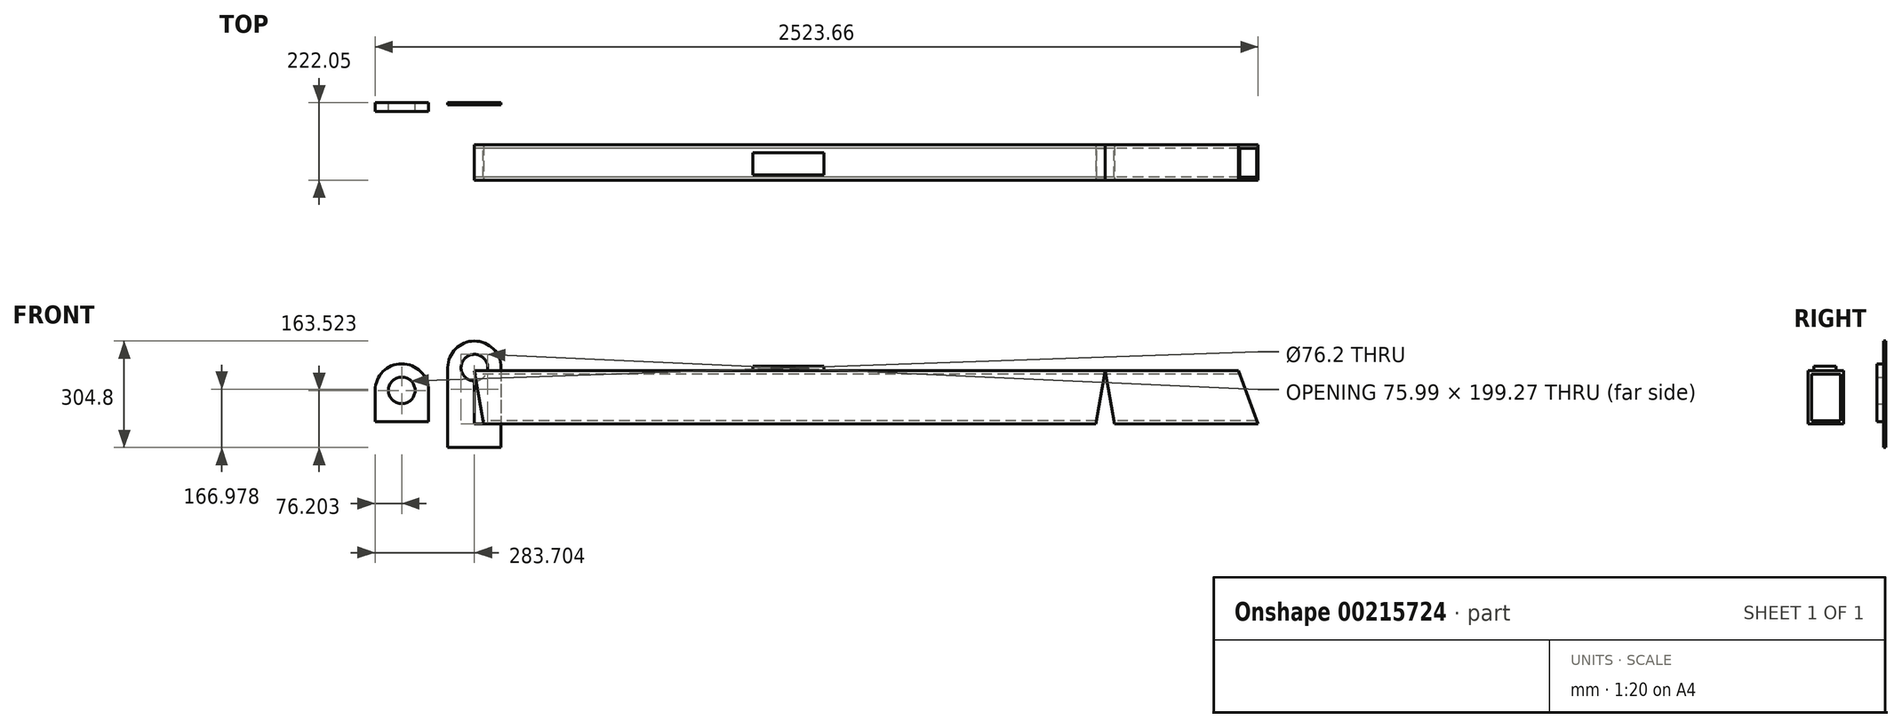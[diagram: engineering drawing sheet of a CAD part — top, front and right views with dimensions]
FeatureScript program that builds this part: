
annotation { "Feature Type Name" : "Feature", "Feature Type Description" : "" }
export const myFeature = defineFeature(function(context is Context, id is Id, definition is map)
    precondition{}
    {
        {
            var Q0;
            Q0=qCreatedBy(makeId("Front.planeOp"),FACE);
            var sketch = newSketch(context, id + "F0", { "sketchPlane" : qUnion([Q0])});
            skLineSegment(sketch, "E0.bottom", {"start": v(0, 152.4) * mm, "end": v(0, 152.4) * mm});
            skLineSegment(sketch, "E0.top", {"start": v(76.2, -152.4) * mm, "end": v(-76.2, -152.4) * mm});
            skLineSegment(sketch, "E0.left", {"start": v(76.2, 76.2) * mm, "end": v(76.2, -152.4) * mm});
            skLineSegment(sketch, "E0.right", {"start": v(-76.2, 76.2) * mm, "end": v(-76.2, -152.4) * mm});
            skPoint(sketch, "E0.middle", {"position": v(0, 0) * mm});
            skPoint(sketch, "E1.visualSharp", {"position": v(-76.2, 152.4) * mm});
            skArc(sketch, "E1.filletArc", {"start": v(0, 152.4) * mm, "mid": v(-53.88, 130.08) * mm, "end": v(-76.2, 76.2) * mm});
            skPoint(sketch, "E2.visualSharp", {"position": v(76.2, 152.4) * mm});
            skArc(sketch, "E2.filletArc", {"start": v(76.2, 76.2) * mm, "mid": v(53.88, 130.08) * mm, "end": v(0, 152.4) * mm});
            skCircle(sketch, "E3", {"center": v(0, 76.2) * mm, "radius": 38.1 * mm});
            skSolve(sketch);
        }
        {
            var Q0;
            Q0 = qSketchRegion(id + "F0", true);
            extrude(context, id + "F1", {"entities" : qUnion([Q0]), "depth" : 6.35 * mm});
        }
        {
            var Q0;
            Q0=qCreatedBy(makeId("Front.planeOp"),FACE);
            var sketch = newSketch(context, id + "F2", { "sketchPlane" : qUnion([Q0])});
            skLineSegment(sketch, "E4", {"start": v(-131.39, -77.78) * mm, "end": v(-131.39, 11.12) * mm});
            skLineSegment(sketch, "E5", {"start": v(-207.59, 87.32) * mm, "end": v(-207.59, 87.32) * mm});
            skLineSegment(sketch, "E6", {"start": v(-283.79, 11.12) * mm, "end": v(-283.79, -77.78) * mm});
            skLineSegment(sketch, "E7", {"start": v(-283.79, -77.78) * mm, "end": v(-131.39, -77.78) * mm});
            skPoint(sketch, "E8.visualSharp", {"position": v(-283.79, 87.32) * mm});
            skArc(sketch, "E8.filletArc", {"start": v(-207.59, 87.32) * mm, "mid": v(-261.47, 65) * mm, "end": v(-283.79, 11.12) * mm});
            skPoint(sketch, "E9.visualSharp", {"position": v(-131.39, 87.32) * mm});
            skArc(sketch, "E9.filletArc", {"start": v(-131.39, 11.12) * mm, "mid": v(-153.7, 65) * mm, "end": v(-207.59, 87.32) * mm});
            skCircle(sketch, "E10", {"center": v(-207.59, 11.12) * mm, "radius": 38.1 * mm});
            skSolve(sketch);
        }
        {
            var Q0;
            Q0=makeQuery(id+"F2.imprint","IMPRINT",FACE,{"disambiguationData":[TD([[makeQuery(id+"F2.imprint","IMPRINT",EDGE,{"derivedFrom":sQuery(id+"F2.wireOp",EDGE,"E4")}),1.0]])]});
            extrude(context, id + "F3", {"entities" : qUnion([Q0]), "depth" : 25.4 * mm});
        }
        {
            var Q0;
            Q0=qCreatedBy(makeId("Right.planeOp"),FACE);
            var sketch = newSketch(context, id + "F4", { "sketchPlane" : qUnion([Q0])});
            skLineSegment(sketch, "E11.bottom", {"start": v(-120.45, 67.34) * mm, "end": v(-222.05, 67.34) * mm});
            skLineSegment(sketch, "E11.top", {"start": v(-120.45, -85.06) * mm, "end": v(-222.05, -85.06) * mm});
            skLineSegment(sketch, "E11.left", {"start": v(-120.45, 67.34) * mm, "end": v(-120.45, -85.06) * mm});
            skLineSegment(sketch, "E11.right", {"start": v(-222.05, 67.34) * mm, "end": v(-222.05, -85.06) * mm});
            skLineSegment(sketch, "E12.0", {"start": v(-129.97, 57.82) * mm, "end": v(-212.52, 57.82) * mm});
            skLineSegment(sketch, "E12.1", {"start": v(-129.97, 57.82) * mm, "end": v(-129.97, -75.53) * mm});
            skLineSegment(sketch, "E12.2", {"start": v(-129.97, -75.53) * mm, "end": v(-212.52, -75.53) * mm});
            skLineSegment(sketch, "E12.3", {"start": v(-212.52, 57.82) * mm, "end": v(-212.52, -75.53) * mm});
            skSolve(sketch);
        }
        {
            var Q0;
            Q0=makeQuery(id+"F4.imprint","IMPRINT",FACE,{"disambiguationData":[TD([[makeQuery(id+"F4.imprint","IMPRINT",EDGE,{"derivedFrom":sQuery(id+"F4.wireOp",EDGE,"E11.bottom")}),1.0]])]});
            extrude(context, id + "F5", {"entities" : qUnion([Q0]), "depth" : 1803.4 * mm});
        }
        {
            var Q0;
            Q0=makeQuery(id+"F5.opExtrude","CAP_FACE",FACE,{"disambiguationData":[OSD([sQuery(id+"F4.wireOp",EDGE,"E11.bottom"),sQuery(id+"F4.wireOp",EDGE,"E11.top"),sQuery(id+"F4.wireOp",EDGE,"E11.left"),sQuery(id+"F4.wireOp",EDGE,"E11.right"),sQuery(id+"F4.wireOp",EDGE,"E12.0"),sQuery(id+"F4.wireOp",EDGE,"E12.1"),sQuery(id+"F4.wireOp",EDGE,"E12.2"),sQuery(id+"F4.wireOp",EDGE,"E12.3")])],"isStart":false});
            extrude(context, id + "F6", {"entities" : qUnion([Q0]), "depth" : 508 * mm});
        }
        {
            var Q0;
            Q0=makeQuery(id+"F6.opExtrude","SWEPT_FACE",FACE,{"disambiguationData":[OSD([sQuery(id+"F4.wireOp",EDGE,"E11.right")])]});
            var sketch = newSketch(context, id + "F7", { "sketchPlane" : qUnion([Q0])});
            skLineSegment(sketch, "E13", {"start": v(1803.4, 67.34) * mm, "end": v(1842.84, -156.32) * mm});
            skLineSegment(sketch, "E14", {"start": v(2254.22, -124.5) * mm, "end": v(2184.4, 67.34) * mm});
            skSolve(sketch);
        }
        {
            var Q0;
            {var subQ1=sQuery(id+"F4.wireOp",EDGE,"E11.right");var subQ2=makeQuery(id+"F6.opExtrude","CAP_EDGE",EDGE,{"disambiguationData":[OSD([subQ1])],"isStart":true});Q0=makeQuery(id+"F7.imprint","IMPRINT",FACE,{"disambiguationData":[TD([[makeQuery(id+"F7.imprint","IMPRINT",EDGE,{"derivedFrom":subQ2}),1.0]])]});}
            var Q1;
            {var subQ1=sQuery(id+"F4.wireOp",EDGE,"E11.right");var subQ6=makeQuery(id+"F6.opExtrude","CAP_EDGE",EDGE,{"disambiguationData":[OSD([subQ1])],"isStart":false});Q1=makeQuery(id+"F7.imprint","IMPRINT",FACE,{"disambiguationData":[TD([[makeQuery(id+"F7.imprint","IMPRINT",EDGE,{"derivedFrom":subQ6}),-1.0]])]});}
            extrude(context, id + "F8", {"entities" : qUnion([Q0, Q1]), "operationType" : NewBodyOperationType.REMOVE, "endBound" : BoundingType.THROUGH_ALL, "oppositeDirection" : true, "depth" : 25.4 * mm});
        }
        {
            var Q0;
            Q0=makeQuery(id+"F5.opExtrude","SWEPT_FACE",FACE,{"disambiguationData":[OSD([sQuery(id+"F4.wireOp",EDGE,"E11.right")])]});
            var sketch = newSketch(context, id + "F9", { "sketchPlane" : qUnion([Q0])});
            skLineSegment(sketch, "E15", {"start": v(1803.4, 67.34) * mm, "end": v(1747.97, -247) * mm});
            skLineSegment(sketch, "E16", {"start": v(0, 67.34) * mm, "end": v(32.38, -116.31) * mm});
            skSolve(sketch);
        }
        {
            var Q0;
            {var subQ1=sQuery(id+"F4.wireOp",EDGE,"E11.right");var subQ2=makeQuery(id+"F5.opExtrude","CAP_EDGE",EDGE,{"disambiguationData":[OSD([subQ1])],"isStart":true});Q0=makeQuery(id+"F9.imprint","IMPRINT",FACE,{"disambiguationData":[TD([[makeQuery(id+"F9.imprint","IMPRINT",EDGE,{"derivedFrom":subQ2}),1.0]])]});}
            var Q1;
            {var subQ1=sQuery(id+"F4.wireOp",EDGE,"E11.right");var subQ2=makeQuery(id+"F5.opExtrude","CAP_EDGE",EDGE,{"disambiguationData":[OSD([subQ1])],"isStart":false});Q1=makeQuery(id+"F9.imprint","IMPRINT",FACE,{"disambiguationData":[TD([[makeQuery(id+"F9.imprint","IMPRINT",EDGE,{"derivedFrom":subQ2}),-1.0]])]});}
            extrude(context, id + "F10", {"entities" : qUnion([Q0, Q1]), "operationType" : NewBodyOperationType.REMOVE, "endBound" : BoundingType.THROUGH_ALL, "oppositeDirection" : true, "depth" : 25.4 * mm});
        }
        {
            var Q0;
            Q0=makeQuery(id+"F5.opExtrude","SWEPT_FACE",FACE,{"disambiguationData":[OSD([sQuery(id+"F4.wireOp",EDGE,"E11.bottom")])]});
            var sketch = newSketch(context, id + "F11", { "sketchPlane" : qUnion([Q0])});
            skLineSegment(sketch, "E17.bottom", {"start": v(795.35, -142.55) * mm, "end": v(998.55, -142.55) * mm});
            skLineSegment(sketch, "E17.top", {"start": v(795.35, -206.05) * mm, "end": v(998.55, -206.05) * mm});
            skLineSegment(sketch, "E17.left", {"start": v(795.35, -142.55) * mm, "end": v(795.35, -206.05) * mm});
            skLineSegment(sketch, "E17.right", {"start": v(998.55, -142.55) * mm, "end": v(998.55, -206.05) * mm});
            skSolve(sketch);
        }
        {
            var Q0;
            Q0 = qSketchRegion(id + "F11", true);
            extrude(context, id + "F12", {"entities" : qUnion([Q0]), "depth" : 12.7 * mm});
        }
    });
